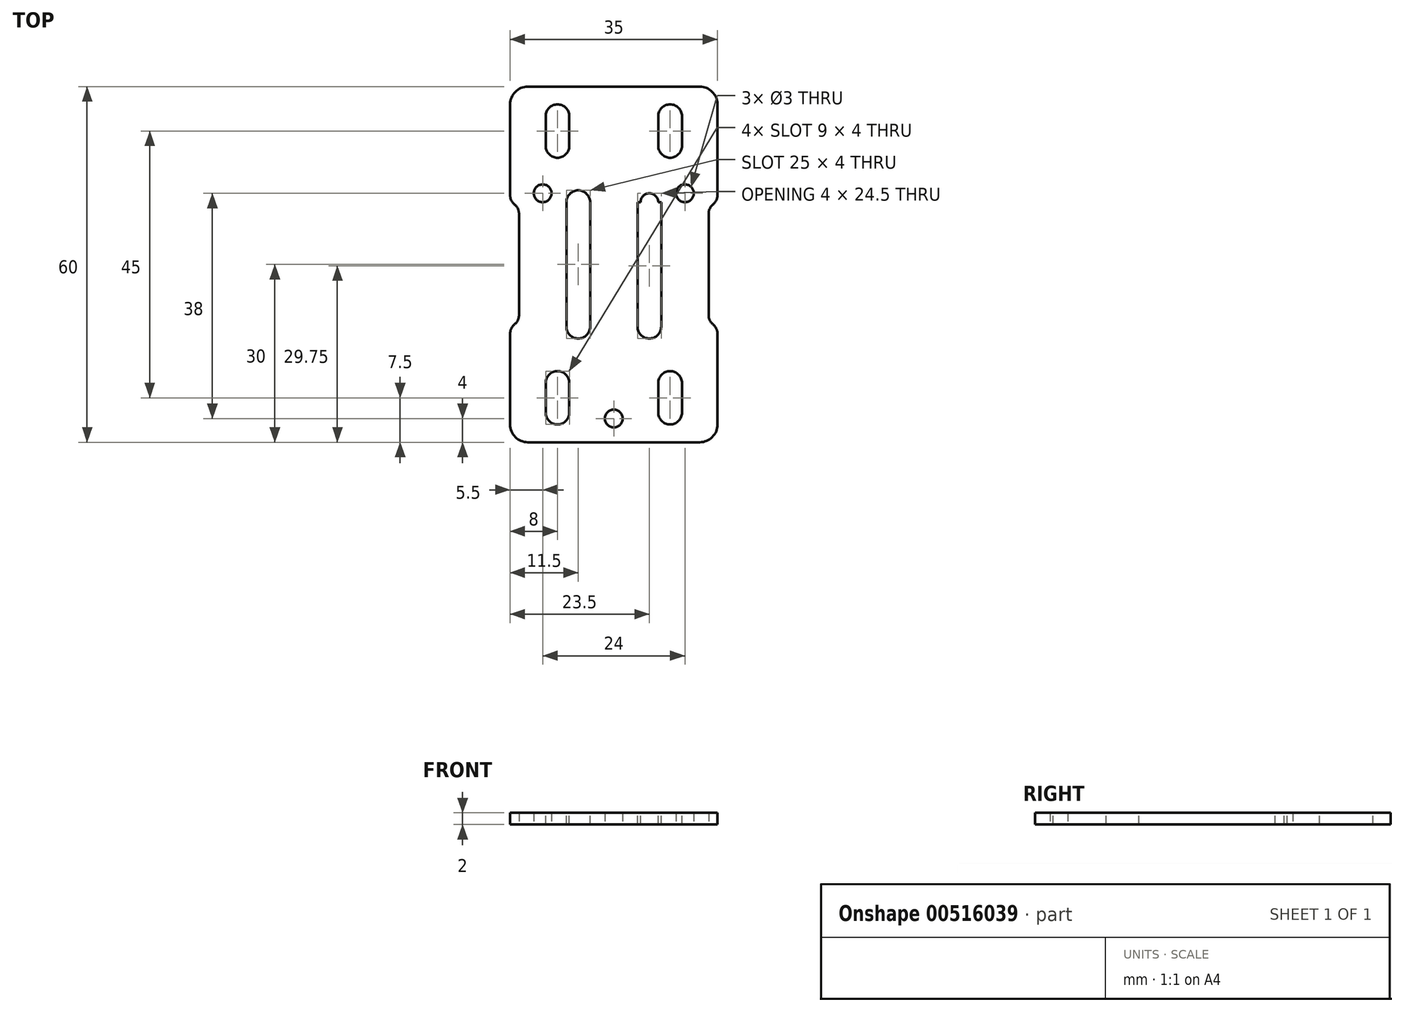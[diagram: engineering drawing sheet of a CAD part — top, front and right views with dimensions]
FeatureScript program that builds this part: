
annotation { "Feature Type Name" : "Feature", "Feature Type Description" : "" }
export const myFeature = defineFeature(function(context is Context, id is Id, definition is map)
    precondition{}
    {
        {
            var Q0;
            Q0=qCreatedBy(makeId("Top.planeOp"),FACE);
            var sketch = newSketch(context, id + "F0", { "sketchPlane" : qUnion([Q0])});
            skLineSegment(sketch, "E0", {"start": v(-17.5, 0) * mm, "end": v(17.5, 0) * mm, "construction": true});
            skLineSegment(sketch, "E1", {"start": v(0, -17.5) * mm, "end": v(0, 17.5) * mm, "construction": true});
            skLineSegment(sketch, "E2.bottom", {"start": v(-17.5, -17.5) * mm, "end": v(17.5, -17.5) * mm, "construction": true});
            skLineSegment(sketch, "E2.top", {"start": v(-17.5, 17.5) * mm, "end": v(17.5, 17.5) * mm, "construction": true});
            skLineSegment(sketch, "E2.left", {"start": v(-17.5, -17.5) * mm, "end": v(-17.5, 17.5) * mm});
            skLineSegment(sketch, "E2.right", {"start": v(17.5, -17.5) * mm, "end": v(17.5, 17.5) * mm});
            skLineSegment(sketch, "E3", {"start": v(-17.5, -17.5) * mm, "end": v(17.5, 17.5) * mm, "construction": true});
            skLineSegment(sketch, "E4", {"start": v(-17.5, 17.5) * mm, "end": v(17.5, -17.5) * mm, "construction": true});
            skLineSegment(sketch, "E5", {"start": v(-12, -12) * mm, "end": v(12, -12) * mm, "construction": true});
            skLineSegment(sketch, "E6", {"start": v(12, -12) * mm, "end": v(12, 12) * mm, "construction": true});
            skLineSegment(sketch, "E7", {"start": v(12, 12) * mm, "end": v(-12, 12) * mm, "construction": true});
            skLineSegment(sketch, "E8", {"start": v(-12, 12) * mm, "end": v(-12, -12) * mm, "construction": true});
            skCircle(sketch, "E9", {"center": v(-12, -12) * mm, "radius": 1.5 * mm, "construction": true});
            skCircle(sketch, "E10", {"center": v(-12, 12) * mm, "radius": 1.5 * mm});
            skCircle(sketch, "E11", {"center": v(12, 12) * mm, "radius": 1.5 * mm});
            skCircle(sketch, "E12", {"center": v(12, -12) * mm, "radius": 1.5 * mm, "construction": true});
            skLineSegment(sketch, "E13", {"start": v(-17.5, -17.5) * mm, "end": v(-17.5, -30) * mm});
            skLineSegment(sketch, "E14", {"start": v(-17.5, -30) * mm, "end": v(17.5, -30) * mm});
            skLineSegment(sketch, "E15", {"start": v(17.5, -30) * mm, "end": v(17.5, -17.5) * mm});
            skLineSegment(sketch, "E16", {"start": v(-17.5, 17.5) * mm, "end": v(-17.5, 30) * mm});
            skLineSegment(sketch, "E17", {"start": v(-17.5, 30) * mm, "end": v(17.5, 30) * mm});
            skLineSegment(sketch, "E18", {"start": v(17.5, 30) * mm, "end": v(17.5, 17.5) * mm});
            skCircle(sketch, "E19", {"center": v(0, -26) * mm, "radius": 1.5 * mm});
            skSolve(sketch);
        }
        {
            var Q0;
            Q0 = qSketchRegion(id + "F0", true);
            extrude(context, id + "F1", {"entities" : qUnion([Q0]), "depth" : 2 * mm, "offsetDistance" : 25 * mm});
        }
        {
            var Q0;
            Q0=makeQuery(id+"F1.opExtrude","SWEPT_EDGE",EDGE,{"disambiguationData":[OSD([sQuery(id+"F0.wireOp",EDGE,"E13"),sQuery(id+"F0.wireOp",EDGE,"E14")])]});
            var Q1;
            Q1=makeQuery(id+"F1.opExtrude","SWEPT_EDGE",EDGE,{"disambiguationData":[OSD([sQuery(id+"F0.wireOp",EDGE,"E14"),sQuery(id+"F0.wireOp",EDGE,"E15")])]});
            var Q2;
            Q2=makeQuery(id+"F1.opExtrude","SWEPT_EDGE",EDGE,{"disambiguationData":[OSD([sQuery(id+"F0.wireOp",EDGE,"E17"),sQuery(id+"F0.wireOp",EDGE,"E18")])]});
            var Q3;
            Q3=makeQuery(id+"F1.opExtrude","SWEPT_EDGE",EDGE,{"disambiguationData":[OSD([sQuery(id+"F0.wireOp",EDGE,"E16"),sQuery(id+"F0.wireOp",EDGE,"E17")])]});
            fillet(context, id + "F2", {"entities" : qUnion([Q0, Q1, Q2, Q3]), "radius" : 3 * mm, "tangentPropagation" : true, "allowEdgeOverflow" : false});
        }
        {
            var Q0;
            Q0=makeQuery(id+"F1.opExtrude","CAP_FACE",FACE,{"disambiguationData":[OSD([sQuery(id+"F0.wireOp",EDGE,"E2.bottom"),sQuery(id+"F0.wireOp",EDGE,"E2.top"),sQuery(id+"F0.wireOp",EDGE,"E2.left"),sQuery(id+"F0.wireOp",EDGE,"E2.right"),sQuery(id+"F0.wireOp",EDGE,"E9"),sQuery(id+"F0.wireOp",EDGE,"E10"),sQuery(id+"F0.wireOp",EDGE,"E11"),sQuery(id+"F0.wireOp",EDGE,"E12")])],"isStart":false});
            var sketch = newSketch(context, id + "F3", { "sketchPlane" : qUnion([Q0])});
            skLineSegment(sketch, "E20.bottom", {"start": v(7.5, 25) * mm, "end": v(11.5, 25) * mm});
            skLineSegment(sketch, "E20.top", {"start": v(7.5, -25) * mm, "end": v(11.5, -25) * mm});
            skLineSegment(sketch, "E20.left", {"start": v(7.5, 25) * mm, "end": v(7.5, 20) * mm});
            skLineSegment(sketch, "E20.right", {"start": v(11.5, 25) * mm, "end": v(11.5, 20) * mm});
            skLineSegment(sketch, "E21.bottom", {"start": v(-11.5, -25) * mm, "end": v(-7.5, -25) * mm});
            skLineSegment(sketch, "E21.top", {"start": v(-11.5, 25) * mm, "end": v(-7.5, 25) * mm});
            skLineSegment(sketch, "E21.left", {"start": v(-11.5, -25) * mm, "end": v(-11.5, -20) * mm});
            skLineSegment(sketch, "E21.right", {"start": v(-7.5, -25) * mm, "end": v(-7.5, -20) * mm});
            skLineSegment(sketch, "E22.bottom", {"start": v(-17.5, -10.5) * mm, "end": v(-16, -10.5) * mm});
            skLineSegment(sketch, "E22.top", {"start": v(-17.5, 10.5) * mm, "end": v(-16, 10.5) * mm});
            skLineSegment(sketch, "E22.left", {"start": v(-17.5, -10.5) * mm, "end": v(-17.5, 10.5) * mm});
            skLineSegment(sketch, "E22.right", {"start": v(-16, -10.5) * mm, "end": v(-16, 10.5) * mm});
            skLineSegment(sketch, "E23.bottom", {"start": v(17.5, -10.5) * mm, "end": v(16, -10.5) * mm});
            skLineSegment(sketch, "E23.top", {"start": v(17.5, 10.5) * mm, "end": v(16, 10.5) * mm});
            skLineSegment(sketch, "E23.left", {"start": v(17.5, -10.5) * mm, "end": v(17.5, 10.5) * mm});
            skLineSegment(sketch, "E23.right", {"start": v(16, -10.5) * mm, "end": v(16, 10.5) * mm});
            skLineSegment(sketch, "E24", {"start": v(-8, -10.5) * mm, "end": v(-4, -10.5) * mm});
            skLineSegment(sketch, "E25", {"start": v(-11.5, -20) * mm, "end": v(-7.5, -20) * mm});
            skLineSegment(sketch, "E26", {"start": v(-8, 10.5) * mm, "end": v(-4, 10.5) * mm});
            skLineSegment(sketch, "E27", {"start": v(-11.5, 20) * mm, "end": v(-7.5, 20) * mm});
            skLineSegment(sketch, "E28.trimOffspring", {"start": v(-11.5, 20) * mm, "end": v(-11.5, 25) * mm});
            skLineSegment(sketch, "E29.trimOffspring", {"start": v(-7.5, 20) * mm, "end": v(-7.5, 25) * mm});
            skLineSegment(sketch, "E30.trimOffspring", {"start": v(7.5, 20) * mm, "end": v(11.5, 20) * mm});
            skLineSegment(sketch, "E31.trimOffspring", {"start": v(4, 10.5) * mm, "end": v(8, 10.5) * mm});
            skLineSegment(sketch, "E32.trimOffspring", {"start": v(4, -10.5) * mm, "end": v(8, -10.5) * mm});
            skLineSegment(sketch, "E33.trimOffspring", {"start": v(7.5, -20) * mm, "end": v(11.5, -20) * mm});
            skLineSegment(sketch, "E34.trimOffspring", {"start": v(-8, -10.5) * mm, "end": v(-8, 10.5) * mm});
            skLineSegment(sketch, "E35.trimOffspring", {"start": v(-4, -10.5) * mm, "end": v(-4, 10.5) * mm});
            skLineSegment(sketch, "E36.trimOffspring", {"start": v(7.5, -20) * mm, "end": v(7.5, -25) * mm});
            skLineSegment(sketch, "E37.trimOffspring", {"start": v(11.5, -20) * mm, "end": v(11.5, -25) * mm});
            skLineSegment(sketch, "E38.trimOffspring", {"start": v(4, 10.5) * mm, "end": v(4, -10.5) * mm});
            skLineSegment(sketch, "E39.trimOffspring", {"start": v(8, 10.5) * mm, "end": v(8, -10.5) * mm});
            skSolve(sketch);
        }
        {
            var Q0;
            Q0 = qSketchRegion(id + "F3", true);
            extrude(context, id + "F4", {"entities" : qUnion([Q0]), "operationType" : NewBodyOperationType.REMOVE, "endBound" : BoundingType.THROUGH_ALL, "oppositeDirection" : true, "depth" : 25 * mm, "offsetDistance" : 25 * mm});
        }
        {
            var Q0;
            Q0=makeQuery(id+"F1.opExtrude","CAP_FACE",FACE,{"disambiguationData":[OSD([sQuery(id+"F0.wireOp",EDGE,"E2.bottom"),sQuery(id+"F0.wireOp",EDGE,"E2.top"),sQuery(id+"F0.wireOp",EDGE,"E2.left"),sQuery(id+"F0.wireOp",EDGE,"E2.right"),sQuery(id+"F0.wireOp",EDGE,"E9"),sQuery(id+"F0.wireOp",EDGE,"E10"),sQuery(id+"F0.wireOp",EDGE,"E11"),sQuery(id+"F0.wireOp",EDGE,"E12")])],"isStart":false});
            var sketch = newSketch(context, id + "F5", { "sketchPlane" : qUnion([Q0])});
            skCircle(sketch, "E40", {"center": v(-9.5, 25) * mm, "radius": 2 * mm});
            skCircle(sketch, "E41", {"center": v(9.5, 25) * mm, "radius": 2 * mm});
            skCircle(sketch, "E42", {"center": v(9.5, -25) * mm, "radius": 2 * mm});
            skCircle(sketch, "E43", {"center": v(-9.5, -25) * mm, "radius": 2 * mm});
            skCircle(sketch, "E44", {"center": v(-9.5, -20) * mm, "radius": 2 * mm});
            skCircle(sketch, "E45", {"center": v(9.5, -20) * mm, "radius": 2 * mm});
            skCircle(sketch, "E46", {"center": v(6, -10.5) * mm, "radius": 2 * mm});
            skCircle(sketch, "E47", {"center": v(-6, -10.5) * mm, "radius": 2 * mm});
            skCircle(sketch, "E48", {"center": v(-6, 10.5) * mm, "radius": 2 * mm});
            skCircle(sketch, "E49", {"center": v(6, 10.5) * mm, "radius": 1.5 * mm});
            skCircle(sketch, "E50", {"center": v(9.5, 20) * mm, "radius": 2 * mm});
            skCircle(sketch, "E51", {"center": v(-9.5, 20) * mm, "radius": 2 * mm});
            skSolve(sketch);
        }
        {
            var Q0;
            Q0 = qSketchRegion(id + "F5", true);
            extrude(context, id + "F6", {"entities" : qUnion([Q0]), "operationType" : NewBodyOperationType.REMOVE, "endBound" : BoundingType.THROUGH_ALL, "oppositeDirection" : true, "depth" : 25 * mm, "offsetDistance" : 25 * mm});
        }
        {
            var Q0;
            Q0=makeQuery(id+"F4.boolean.opBoolean","COPY",EDGE,{"derivedFrom":makeQuery(id+"F4.opExtrude","SWEPT_EDGE",EDGE,{"disambiguationData":[OSD([sQuery(id+"F3.wireOp",EDGE,"E22.bottom"),sQuery(id+"F3.wireOp",EDGE,"E22.right")])]})});
            var Q1;
            Q1=makeQuery(id+"F4.boolean.opBoolean","COPY",EDGE,{"derivedFrom":makeQuery(id+"F4.opExtrude","SWEPT_EDGE",EDGE,{"disambiguationData":[OSD([sQuery(id+"F3.wireOp",EDGE,"E22.top"),sQuery(id+"F3.wireOp",EDGE,"E22.right")])]})});
            var Q2;
            Q2=makeQuery(id+"F4.boolean.opBoolean","COPY",EDGE,{"derivedFrom":makeQuery(id+"F4.opExtrude","SWEPT_EDGE",EDGE,{"disambiguationData":[OSD([sQuery(id+"F3.wireOp",EDGE,"E23.top"),sQuery(id+"F3.wireOp",EDGE,"E23.right")])]})});
            var Q3;
            Q3=makeQuery(id+"F4.boolean.opBoolean","COPY",EDGE,{"derivedFrom":makeQuery(id+"F4.opExtrude","SWEPT_EDGE",EDGE,{"disambiguationData":[OSD([sQuery(id+"F3.wireOp",EDGE,"E23.bottom"),sQuery(id+"F3.wireOp",EDGE,"E23.right")])]})});
            fillet(context, id + "F7", {"entities" : qUnion([Q0, Q1, Q2, Q3]), "radius" : 2 * mm, "tangentPropagation" : true, "allowEdgeOverflow" : false});
        }
        {
            var Q0;
            {var subQ0=sQuery(id+"F0.wireOp",EDGE,"E18");var subQ3=sQuery(id+"F0.wireOp",EDGE,"E15");var subQ10=sQuery(id+"F0.wireOp",EDGE,"E2.right");var subQ12=sQuery(id+"F3.wireOp",EDGE,"E23.bottom");Q0=makeQuery(id+"F7.opFillet","BLEND_EDGE",EDGE,{"blendedFrom":[makeQuery(id+"F4.boolean.opBoolean","COPY",EDGE,{"derivedFrom":makeQuery(id+"F4.opExtrude","SWEPT_EDGE",EDGE,{"disambiguationData":[OSD([subQ12,sQuery(id+"F3.wireOp",EDGE,"E23.right")])]})}),makeQuery(id+"F4.boolean.opBoolean","SPLIT",FACE,{"disambiguationData":[TD([makeQuery(id+"F4.opExtrude","SWEPT_FACE",FACE,{"disambiguationData":[OSD([subQ12])]})])],"derivedFrom":makeQuery(id+"F1.opExtrude","SWEPT_FACE",FACE,{"disambiguationData":[OSD([subQ10,subQ3,subQ0])]})})],"blendedInto":[makeQuery(id+"F4.boolean.opBoolean","SPLIT",FACE,{"disambiguationData":[TD([makeQuery(id+"F4.opExtrude","SWEPT_FACE",FACE,{"disambiguationData":[OSD([subQ12])]})])],"derivedFrom":makeQuery(id+"F1.opExtrude","SWEPT_FACE",FACE,{"disambiguationData":[OSD([subQ10,subQ3,subQ0])]})})]});}
            var Q1;
            {var subQ0=sQuery(id+"F0.wireOp",EDGE,"E18");var subQ3=sQuery(id+"F0.wireOp",EDGE,"E15");var subQ10=sQuery(id+"F0.wireOp",EDGE,"E2.right");var subQ12=sQuery(id+"F3.wireOp",EDGE,"E23.top");Q1=makeQuery(id+"F7.opFillet","BLEND_EDGE",EDGE,{"blendedFrom":[makeQuery(id+"F4.boolean.opBoolean","COPY",EDGE,{"derivedFrom":makeQuery(id+"F4.opExtrude","SWEPT_EDGE",EDGE,{"disambiguationData":[OSD([subQ12,sQuery(id+"F3.wireOp",EDGE,"E23.right")])]})}),makeQuery(id+"F4.boolean.opBoolean","SPLIT",FACE,{"disambiguationData":[TD([makeQuery(id+"F4.opExtrude","SWEPT_FACE",FACE,{"disambiguationData":[OSD([subQ12])]})])],"derivedFrom":makeQuery(id+"F1.opExtrude","SWEPT_FACE",FACE,{"disambiguationData":[OSD([subQ10,subQ3,subQ0])]})})],"blendedInto":[makeQuery(id+"F4.boolean.opBoolean","SPLIT",FACE,{"disambiguationData":[TD([makeQuery(id+"F4.opExtrude","SWEPT_FACE",FACE,{"disambiguationData":[OSD([subQ12])]})])],"derivedFrom":makeQuery(id+"F1.opExtrude","SWEPT_FACE",FACE,{"disambiguationData":[OSD([subQ10,subQ3,subQ0])]})})]});}
            var Q2;
            {var subQ2=sQuery(id+"F0.wireOp",EDGE,"E16");var subQ5=sQuery(id+"F0.wireOp",EDGE,"E13");var subQ11=sQuery(id+"F0.wireOp",EDGE,"E2.left");var subQ12=sQuery(id+"F3.wireOp",EDGE,"E22.bottom");Q2=makeQuery(id+"F7.opFillet","BLEND_EDGE",EDGE,{"blendedFrom":[makeQuery(id+"F4.boolean.opBoolean","COPY",EDGE,{"derivedFrom":makeQuery(id+"F4.opExtrude","SWEPT_EDGE",EDGE,{"disambiguationData":[OSD([subQ12,sQuery(id+"F3.wireOp",EDGE,"E22.right")])]})}),makeQuery(id+"F4.boolean.opBoolean","SPLIT",FACE,{"disambiguationData":[TD([makeQuery(id+"F4.opExtrude","SWEPT_FACE",FACE,{"disambiguationData":[OSD([subQ12])]})])],"derivedFrom":makeQuery(id+"F1.opExtrude","SWEPT_FACE",FACE,{"disambiguationData":[OSD([subQ11,subQ5,subQ2])]})})],"blendedInto":[makeQuery(id+"F4.boolean.opBoolean","SPLIT",FACE,{"disambiguationData":[TD([makeQuery(id+"F4.opExtrude","SWEPT_FACE",FACE,{"disambiguationData":[OSD([subQ12])]})])],"derivedFrom":makeQuery(id+"F1.opExtrude","SWEPT_FACE",FACE,{"disambiguationData":[OSD([subQ11,subQ5,subQ2])]})})]});}
            var Q3;
            {var subQ2=sQuery(id+"F0.wireOp",EDGE,"E16");var subQ5=sQuery(id+"F0.wireOp",EDGE,"E13");var subQ11=sQuery(id+"F0.wireOp",EDGE,"E2.left");var subQ12=sQuery(id+"F3.wireOp",EDGE,"E22.top");Q3=makeQuery(id+"F7.opFillet","BLEND_EDGE",EDGE,{"blendedFrom":[makeQuery(id+"F4.boolean.opBoolean","COPY",EDGE,{"derivedFrom":makeQuery(id+"F4.opExtrude","SWEPT_EDGE",EDGE,{"disambiguationData":[OSD([subQ12,sQuery(id+"F3.wireOp",EDGE,"E22.right")])]})}),makeQuery(id+"F4.boolean.opBoolean","SPLIT",FACE,{"disambiguationData":[TD([makeQuery(id+"F4.opExtrude","SWEPT_FACE",FACE,{"disambiguationData":[OSD([subQ12])]})])],"derivedFrom":makeQuery(id+"F1.opExtrude","SWEPT_FACE",FACE,{"disambiguationData":[OSD([subQ11,subQ5,subQ2])]})})],"blendedInto":[makeQuery(id+"F4.boolean.opBoolean","SPLIT",FACE,{"disambiguationData":[TD([makeQuery(id+"F4.opExtrude","SWEPT_FACE",FACE,{"disambiguationData":[OSD([subQ12])]})])],"derivedFrom":makeQuery(id+"F1.opExtrude","SWEPT_FACE",FACE,{"disambiguationData":[OSD([subQ11,subQ5,subQ2])]})})]});}
            fillet(context, id + "F8", {"entities" : qUnion([Q0, Q1, Q2, Q3]), "radius" : 2 * mm, "tangentPropagation" : true, "allowEdgeOverflow" : false});
        }
    });
